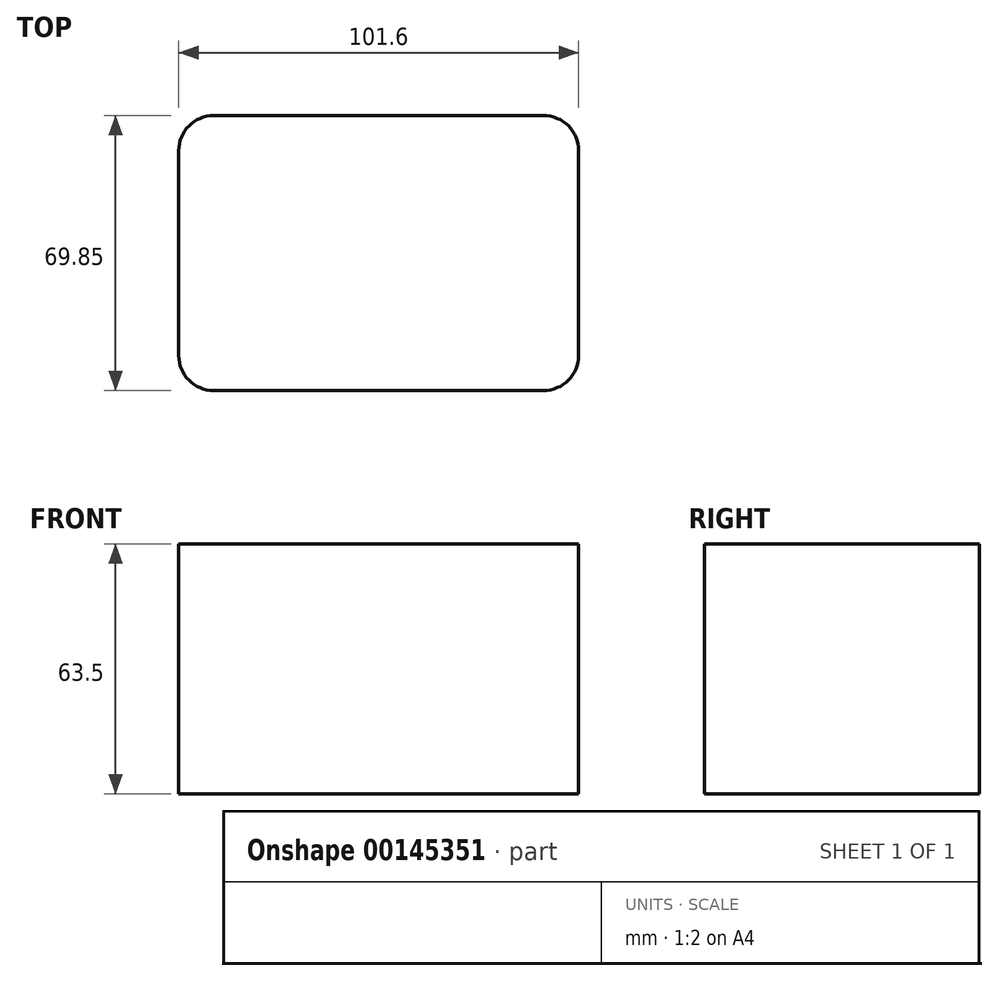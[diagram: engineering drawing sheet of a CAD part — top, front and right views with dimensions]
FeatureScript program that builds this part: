
annotation { "Feature Type Name" : "Feature", "Feature Type Description" : "" }
export const myFeature = defineFeature(function(context is Context, id is Id, definition is map)
    precondition{}
    {
        {
            var Q0;
            Q0=qCreatedBy(makeId("Top.planeOp"),FACE);
            var sketch = newSketch(context, id + "F0", { "sketchPlane" : qUnion([Q0])});
            skLineSegment(sketch, "E0.bottom", {"start": v(-39.9, 33.98) * mm, "end": v(43.91, 33.98) * mm});
            skLineSegment(sketch, "E0.top", {"start": v(-39.9, -35.87) * mm, "end": v(43.91, -35.87) * mm});
            skLineSegment(sketch, "E0.left", {"start": v(-48.8, 25.09) * mm, "end": v(-48.8, -26.98) * mm});
            skLineSegment(sketch, "E0.right", {"start": v(52.8, 25.09) * mm, "end": v(52.8, -26.98) * mm});
            skPoint(sketch, "E1.visualSharp", {"position": v(-48.8, 33.98) * mm});
            skArc(sketch, "E1.filletArc", {"start": v(-39.9, 33.98) * mm, "mid": v(-46.2, 31.38) * mm, "end": v(-48.8, 25.09) * mm});
            skPoint(sketch, "E2.visualSharp", {"position": v(52.8, 33.98) * mm});
            skArc(sketch, "E2.filletArc", {"start": v(52.8, 25.09) * mm, "mid": v(50.2, 31.38) * mm, "end": v(43.91, 33.98) * mm});
            skPoint(sketch, "E3.visualSharp", {"position": v(52.8, -35.87) * mm});
            skArc(sketch, "E3.filletArc", {"start": v(43.91, -35.87) * mm, "mid": v(50.2, -33.27) * mm, "end": v(52.8, -26.98) * mm});
            skPoint(sketch, "E4.visualSharp", {"position": v(-48.8, -35.87) * mm});
            skArc(sketch, "E4.filletArc", {"start": v(-48.8, -26.98) * mm, "mid": v(-46.2, -33.27) * mm, "end": v(-39.9, -35.87) * mm});
            skSolve(sketch);
        }
        {
            var Q0;
            Q0=makeQuery(id+"F0.imprint","IMPRINT",FACE,{"disambiguationData":[TD([[makeQuery(id+"F0.imprint","IMPRINT",EDGE,{"derivedFrom":sQuery(id+"F0.wireOp",EDGE,"E0.bottom")}),-1.0]])]});
            extrude(context, id + "F1", {"entities" : qUnion([Q0]), "depth" : 63.5 * mm});
        }
    });
